# Revit family: KEUCO_14963010000
name_source: partatom
category: Sonderausstattung
revit_build: Autodesk Revit 2016 (Build: 20150220_1215(x64)
units: mm (PartAtom-declared; Revit-internal decimal feet)

## family parameters
Arbeitsebenenbasiert = Nein
Beim Laden mit Abzugskörper schneiden = Nein
Bemaßung runder Anschluss = Durchmesser verwenden
Gemeinsam genutzt = Nein
Immer vertikal = Ja
Raumberechnungspunkt = Nein
Teiletyp = Normal

## types (3) — shared parameters
Beschreibung = --
Gewicht = 382
Hersteller = KEUCO
Kategorie = ACC
Preisgruppe = 1
Serie = Plan
URL = https://www.keuco.com
Verwendung = GWC / WC

## per-type parameters (varying)
| type | Ausschreibungstext |
| 14963010000 | KEUCO PLAN Toilettenpapier-Ersatzrollenhalter 14963010000
Hochglanzverchromter Ersatzrollenhalter 
in ästhetischem, funktionalem Design
zur Wandmontage, mit runder Rosettenkappe, 
Durchmesser 55 mm
leicht zu reinigen
Ausladung 120 mm
Der Toilettenpapier-Ersatzrollenhalter wird verdeckt angebracht
Lieferung inkl. korrosionsfreiem Befestigungsmaterial |
| 14963070000 | KEUCO PLAN Toilettenpapier-Ersatzrollenhalter 14963070000
Toilettenpapier-Ersatzrollenhalter aus hochwertigem Edelstahl 
in ästhetischem, funktionalem Design zur Wandmontage
mit runder Rosettenkappe, Durchmesser 55 mm
leicht zu reinigen
Ausladung 120 mm
Der Toilettenpapier-Ersatzrollenhalter wird verdeckt angebracht
Lieferung inkl. korrosionsfreiem Befestigungsmaterial |
| 14963170000 | KEUCO PLAN Toilettenpapier-Ersatzrollenhalter 14963170000
Toilettenpapier-Ersatzrollenhalter 
aus silber-eloxiertem Aluminium (E6 EV1)/verchromt
in ästhetischem, funktionalem Design, zur Wandmontage
mit runder Rosettenkappe, Durchmesser 55 mm
hochglanzverchromtes Abschlussstück
leicht zu reinigen, Ausladung 120 mm
Der Toilettenpapier-Ersatzrollenhalter wird verdeckt angebracht
Lieferung inkl. korrosionsfreiem Befestigungsmaterial |

note: column(s) folded — value = type name in every type: Artikelnummer

## geometry (parser evidence)
native form markers: Blend x2, Sweep x3
no freeform markers — native parametric forms only
